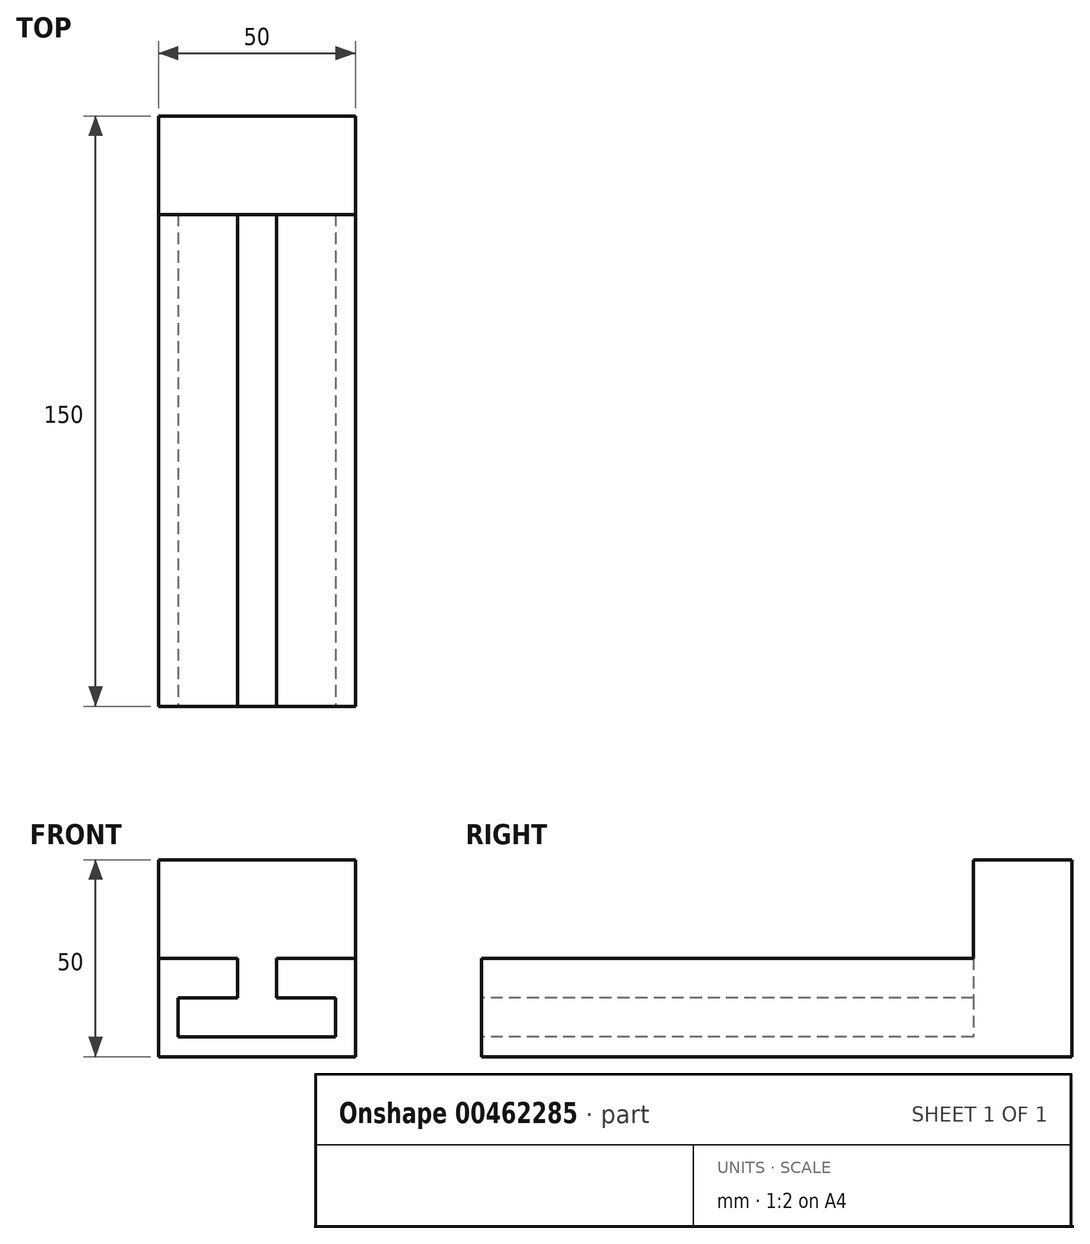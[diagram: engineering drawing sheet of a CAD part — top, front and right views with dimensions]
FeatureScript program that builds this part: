
annotation { "Feature Type Name" : "Feature", "Feature Type Description" : "" }
export const myFeature = defineFeature(function(context is Context, id is Id, definition is map)
    precondition{}
    {
        {
            var Q0;
            Q0=qCreatedBy(makeId("Top.planeOp"),FACE);
            var sketch = newSketch(context, id + "F0", { "sketchPlane" : qUnion([Q0])});
            skLineSegment(sketch, "E0.bottom", {"start": v(25, -75) * mm, "end": v(-25, -75) * mm});
            skLineSegment(sketch, "E0.top", {"start": v(25, 75) * mm, "end": v(-25, 75) * mm});
            skLineSegment(sketch, "E0.left", {"start": v(25, -75) * mm, "end": v(25, 75) * mm});
            skLineSegment(sketch, "E0.right", {"start": v(-25, -75) * mm, "end": v(-25, 75) * mm});
            skPoint(sketch, "E0.middle", {"position": v(0, 0) * mm});
            skSolve(sketch);
        }
        {
            var Q0;
            Q0=makeQuery(id+"F0.imprint","IMPRINT",FACE,{"disambiguationData":[TD([[makeQuery(id+"F0.imprint","IMPRINT",EDGE,{"derivedFrom":sQuery(id+"F0.wireOp",EDGE,"E0.bottom")}),-1.0]])]});
            extrude(context, id + "F1", {"entities" : qUnion([Q0]), "depth" : 25 * mm});
        }
        {
            var Q0;
            Q0=makeQuery(id+"F1.opExtrude","SWEPT_FACE",FACE,{"disambiguationData":[OSD([sQuery(id+"F0.wireOp",EDGE,"E0.bottom")])]});
            var sketch = newSketch(context, id + "F2", { "sketchPlane" : qUnion([Q0])});
            skLineSegment(sketch, "E1", {"start": v(0, 25) * mm, "end": v(5, 25) * mm});
            skLineSegment(sketch, "E2", {"start": v(5, 25) * mm, "end": v(5, 15) * mm});
            skLineSegment(sketch, "E3", {"start": v(5, 15) * mm, "end": v(20, 15) * mm});
            skLineSegment(sketch, "E4", {"start": v(20, 15) * mm, "end": v(20, 5) * mm});
            skLineSegment(sketch, "E5", {"start": v(20, 5) * mm, "end": v(0, 5) * mm});
            skLineSegment(sketch, "E6.MirrorCS", {"start": v(0, 25) * mm, "end": v(-5, 25) * mm});
            skLineSegment(sketch, "E7.MirrorCS", {"start": v(-5, 25) * mm, "end": v(-5, 15) * mm});
            skLineSegment(sketch, "E8.MirrorCS", {"start": v(-5, 15) * mm, "end": v(-20, 15) * mm});
            skLineSegment(sketch, "E9.MirrorCS", {"start": v(-20, 15) * mm, "end": v(-20, 5) * mm});
            skLineSegment(sketch, "E10.MirrorCS", {"start": v(-20, 5) * mm, "end": v(0, 5) * mm});
            skSolve(sketch);
        }
        {
            var Q0;
            Q0=makeQuery(id+"F2.imprint","IMPRINT",FACE,{"disambiguationData":[TD([[makeQuery(id+"F2.imprint","IMPRINT",EDGE,{"derivedFrom":sQuery(id+"F2.wireOp",EDGE,"E1")}),1.0]])]});
            extrude(context, id + "F3", {"entities" : qUnion([Q0]), "operationType" : NewBodyOperationType.REMOVE, "oppositeDirection" : true, "depth" : 125 * mm});
        }
        {
            var Q0;
            Q0=makeQuery(id+"F1.opExtrude","CAP_FACE",FACE,{"disambiguationData":[OSD([sQuery(id+"F0.wireOp",EDGE,"E0.bottom"),sQuery(id+"F0.wireOp",EDGE,"E0.top"),sQuery(id+"F0.wireOp",EDGE,"E0.left"),sQuery(id+"F0.wireOp",EDGE,"E0.right")])],"isStart":false});
            var sketch = newSketch(context, id + "F4", { "sketchPlane" : qUnion([Q0])});
            skLineSegment(sketch, "E11", {"start": v(-5, 50) * mm, "end": v(-25, 50) * mm});
            skLineSegment(sketch, "E12", {"start": v(-25, 50) * mm, "end": v(25, 50) * mm});
            skSolve(sketch);
        }
        {
            var Q0;
            {var subQ0=makeQuery(id+"F1.opExtrude","CAP_EDGE",EDGE,{"disambiguationData":[OSD([sQuery(id+"F0.wireOp",EDGE,"E0.top")])],"isStart":false});Q0=makeQuery(id+"F4.imprint","IMPRINT",FACE,{"disambiguationData":[TD([[makeQuery(id+"F4.imprint","IMPRINT",EDGE,{"derivedFrom":subQ0}),1.0]])]});}
            extrude(context, id + "F5", {"entities" : qUnion([Q0]), "operationType" : NewBodyOperationType.ADD, "depth" : 25 * mm});
        }
    });
